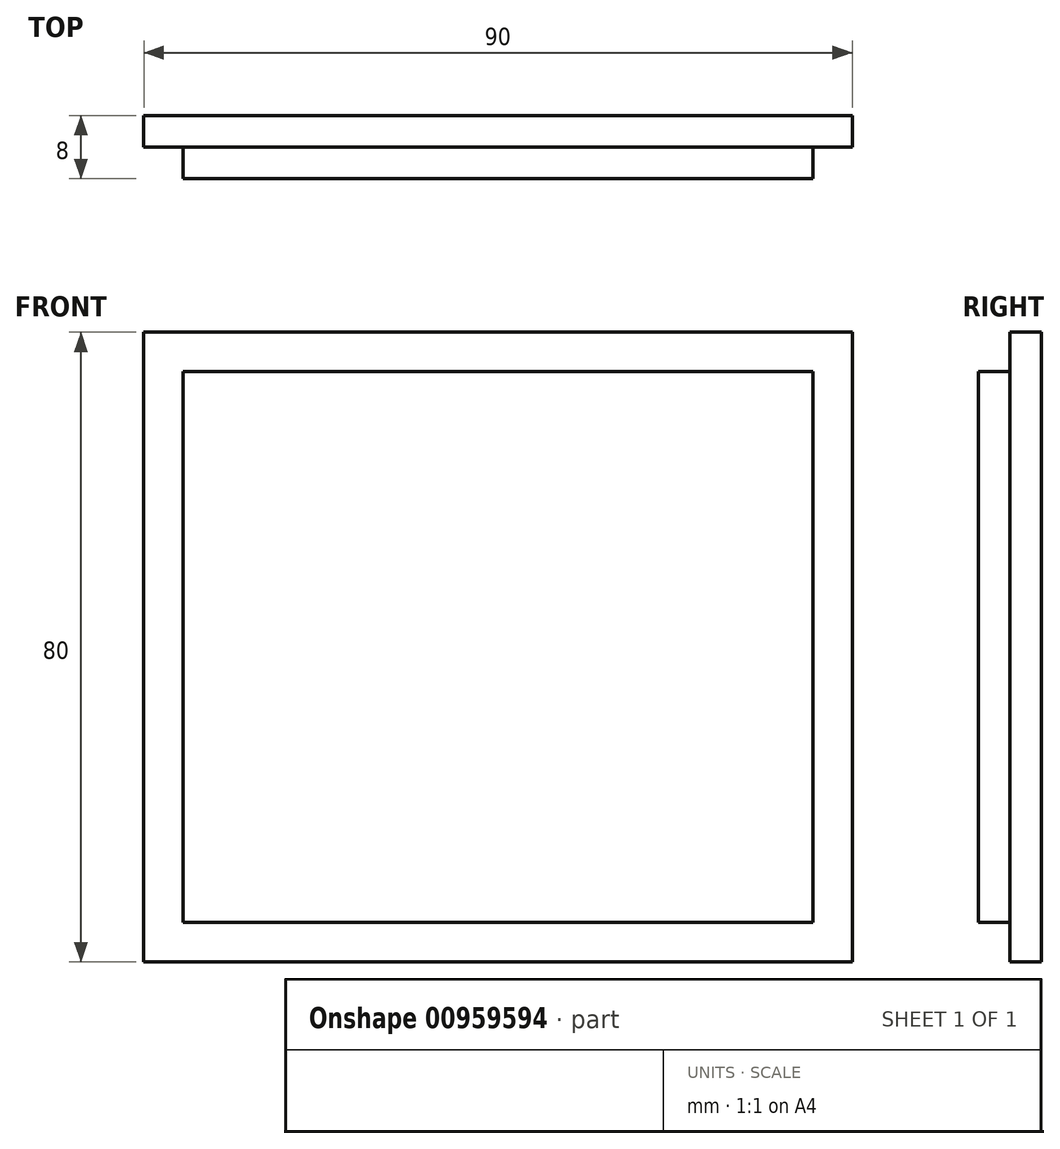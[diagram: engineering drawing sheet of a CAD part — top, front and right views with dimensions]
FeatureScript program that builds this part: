
annotation { "Feature Type Name" : "Feature", "Feature Type Description" : "" }
export const myFeature = defineFeature(function(context is Context, id is Id, definition is map)
    precondition{}
    {
        {
            var Q0;
            Q0=qCreatedBy(makeId("Front.planeOp"),FACE);
            var sketch = newSketch(context, id + "F0", { "sketchPlane" : qUnion([Q0])});
            skLineSegment(sketch, "E0.bottom", {"start": v(-65, 55.4) * mm, "end": v(15, 55.4) * mm});
            skLineSegment(sketch, "E0.top", {"start": v(-65, -14.6) * mm, "end": v(15, -14.6) * mm});
            skLineSegment(sketch, "E0.left", {"start": v(-65, 55.4) * mm, "end": v(-65, -14.6) * mm});
            skLineSegment(sketch, "E0.right", {"start": v(15, 55.4) * mm, "end": v(15, -14.6) * mm});
            skLineSegment(sketch, "E1.0", {"start": v(-70, 60.4) * mm, "end": v(20, 60.4) * mm});
            skLineSegment(sketch, "E1.1", {"start": v(-70, 60.4) * mm, "end": v(-70, -19.6) * mm});
            skLineSegment(sketch, "E1.2", {"start": v(-70, -19.6) * mm, "end": v(20, -19.6) * mm});
            skLineSegment(sketch, "E1.3", {"start": v(20, 60.4) * mm, "end": v(20, -19.6) * mm});
            skSolve(sketch);
        }
        {
            var Q0;
            Q0=makeQuery(id+"F0.imprint","IMPRINT",FACE,{"disambiguationData":[TD([[makeQuery(id+"F0.imprint","IMPRINT",EDGE,{"derivedFrom":sQuery(id+"F0.wireOp",EDGE,"E0.bottom")}),-1.0]])]});
            extrude(context, id + "F1", {"entities" : qUnion([Q0]), "depth" : 8 * mm, "offsetDistance" : 25 * mm});
        }
        {
            var Q0;
            Q0=makeQuery(id+"F0.imprint","IMPRINT",FACE,{"disambiguationData":[TD([[makeQuery(id+"F0.imprint","IMPRINT",EDGE,{"derivedFrom":sQuery(id+"F0.wireOp",EDGE,"E0.bottom")}),1.0]])]});
            extrude(context, id + "F2", {"entities" : qUnion([Q0]), "operationType" : NewBodyOperationType.ADD, "depth" : 4 * mm, "offsetDistance" : 25 * mm});
        }
    });
